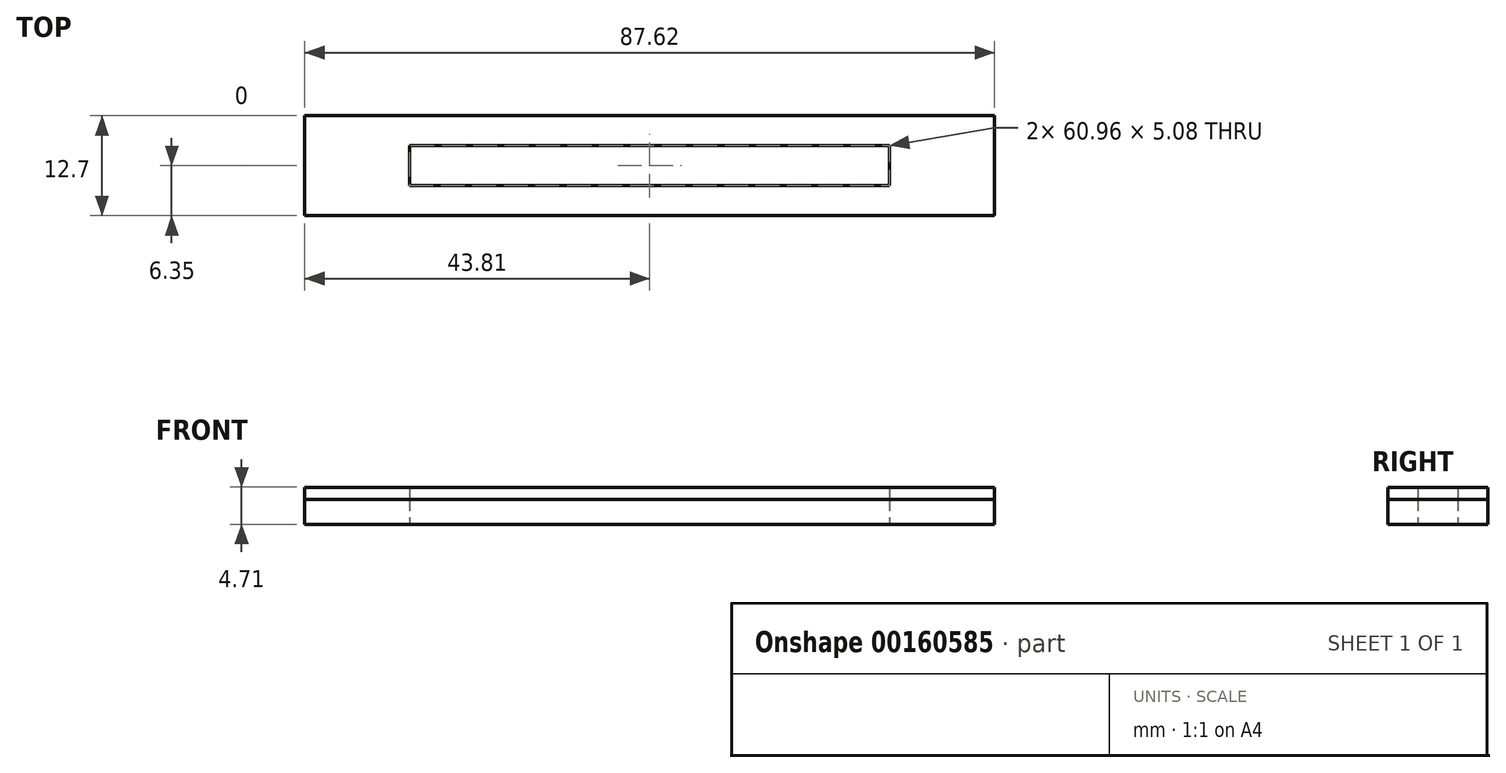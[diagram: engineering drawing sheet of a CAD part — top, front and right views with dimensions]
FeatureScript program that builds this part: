
annotation { "Feature Type Name" : "Feature", "Feature Type Description" : "" }
export const myFeature = defineFeature(function(context is Context, id is Id, definition is map)
    precondition{}
    {
        {
            var Q0;
            Q0=qCreatedBy(makeId("Top.planeOp"),FACE);
            var sketch = newSketch(context, id + "F0", { "sketchPlane" : qUnion([Q0])});
            skLineSegment(sketch, "E0.bottom", {"start": v(66.04, 6.35) * mm, "end": v(-66.04, 6.35) * mm});
            skLineSegment(sketch, "E0.top", {"start": v(66.04, -6.35) * mm, "end": v(-66.04, -6.35) * mm});
            skLineSegment(sketch, "E0.left", {"start": v(66.04, 6.35) * mm, "end": v(66.04, -6.35) * mm});
            skLineSegment(sketch, "E0.right", {"start": v(-66.04, 6.35) * mm, "end": v(-66.04, -6.35) * mm});
            skPoint(sketch, "E0.middle", {"position": v(0, 0) * mm});
            skSolve(sketch);
        }
        {
            var Q0;
            Q0 = qSketchRegion(id + "F0", true);
            extrude(context, id + "F1", {"entities" : qUnion([Q0]), "oppositeDirection" : true, "depth" : 3.17 * mm});
        }
        {
            var Q0;
            Q0=makeQuery(id+"F1.opExtrude","CAP_FACE",FACE,{"disambiguationData":[OSD([sQuery(id+"F0.wireOp",EDGE,"E0.bottom"),sQuery(id+"F0.wireOp",EDGE,"E0.top"),sQuery(id+"F0.wireOp",EDGE,"E0.left"),sQuery(id+"F0.wireOp",EDGE,"E0.right")])],"isStart":true});
            extrude(context, id + "F2", {"entities" : qUnion([Q0]), "depth" : (1.4 + (1 / 8)) * mm});
        }
        {
            var Q0;
            Q0=makeQuery(id+"F2.opExtrude","CAP_FACE",FACE,{"disambiguationData":[OSD([sQuery(id+"F0.wireOp",EDGE,"E0.bottom"),sQuery(id+"F0.wireOp",EDGE,"E0.top"),sQuery(id+"F0.wireOp",EDGE,"E0.left"),sQuery(id+"F0.wireOp",EDGE,"E0.right")])],"isStart":false});
            var sketch = newSketch(context, id + "F3", { "sketchPlane" : qUnion([Q0])});
            skLineSegment(sketch, "E1.bottom", {"start": v(43.82, 6.35) * mm, "end": v(-43.81, 6.35) * mm});
            skLineSegment(sketch, "E1.top", {"start": v(43.82, -6.35) * mm, "end": v(-43.81, -6.35) * mm});
            skLineSegment(sketch, "E1.left", {"start": v(43.82, 6.35) * mm, "end": v(43.82, -6.35) * mm});
            skLineSegment(sketch, "E1.right", {"start": v(-43.81, 6.35) * mm, "end": v(-43.81, -6.35) * mm});
            skSolve(sketch);
        }
        {
            var Q0;
            {var subQ0=sQuery(id+"F3.wireOp",EDGE,"E1.right");Q0=makeQuery(id+"F3.imprint","IMPRINT",FACE,{"disambiguationData":[TD([[makeQuery(id+"F3.imprint","IMPRINT",EDGE,{"derivedFrom":subQ0}),-1.0]])]});}
            var Q1;
            {var subQ0=sQuery(id+"F3.wireOp",EDGE,"E1.left");Q1=makeQuery(id+"F3.imprint","IMPRINT",FACE,{"disambiguationData":[TD([[makeQuery(id+"F3.imprint","IMPRINT",EDGE,{"derivedFrom":subQ0}),1.0]])]});}
            extrude(context, id + "F4", {"entities" : qUnion([Q0, Q1]), "operationType" : NewBodyOperationType.REMOVE, "oppositeDirection" : true, "depth" : 35.56 * mm});
        }
        {
            var Q0;
            Q0=makeQuery(id+"F2.opExtrude","SWEPT_FACE",FACE,{"disambiguationData":[OSD([sQuery(id+"F0.wireOp",EDGE,"E0.top")])]});
            var sketch = newSketch(context, id + "F5", { "sketchPlane" : qUnion([Q0])});
            skLineSegment(sketch, "E2.bottom", {"start": v(40.64, 35.56) * mm, "end": v(-40.64, 35.56) * mm});
            skLineSegment(sketch, "E2.top", {"start": v(40.64, 0) * mm, "end": v(-40.64, 0) * mm});
            skLineSegment(sketch, "E2.left", {"start": v(40.64, 35.56) * mm, "end": v(40.64, 0) * mm});
            skLineSegment(sketch, "E2.right", {"start": v(-40.64, 35.56) * mm, "end": v(-40.64, 0) * mm});
            skSolve(sketch);
        }
        {
            var Q0;
            Q0=makeQuery(id+"F5.imprint","IMPRINT",FACE,{"disambiguationData":[TD([[makeQuery(id+"F5.imprint","IMPRINT",EDGE,{"derivedFrom":sQuery(id+"F5.wireOp",EDGE,"E2.bottom")}),1.0]])]});
            extrude(context, id + "F6", {"entities" : qUnion([Q0]), "operationType" : NewBodyOperationType.REMOVE, "endBound" : BoundingType.THROUGH_ALL, "oppositeDirection" : true, "depth" : 25.4 * mm});
        }
        {
            var Q0;
            Q0=qCreatedBy(makeId("Top.planeOp"),FACE);
            var sketch = newSketch(context, id + "F7", { "sketchPlane" : qUnion([Q0])});
            skLineSegment(sketch, "E3.bottom", {"start": v(30.48, 2.54) * mm, "end": v(-30.48, 2.54) * mm});
            skLineSegment(sketch, "E3.top", {"start": v(30.48, -2.54) * mm, "end": v(-30.48, -2.54) * mm});
            skLineSegment(sketch, "E3.left", {"start": v(30.48, 2.54) * mm, "end": v(30.48, -2.54) * mm});
            skLineSegment(sketch, "E3.right", {"start": v(-30.48, 2.54) * mm, "end": v(-30.48, -2.54) * mm});
            skPoint(sketch, "E3.middle", {"position": v(0, 0) * mm});
            skCircle(sketch, "E4", {"center": v(55.88, 0) * mm, "radius": 3.18 * mm});
            skCircle(sketch, "E5", {"center": v(-55.88, 0) * mm, "radius": 3.18 * mm});
            skSolve(sketch);
        }
        {
            var Q0;
            Q0=makeQuery(id+"F7.imprint","IMPRINT",FACE,{"disambiguationData":[TD([[makeQuery(id+"F7.imprint","IMPRINT",EDGE,{"derivedFrom":sQuery(id+"F7.wireOp",EDGE,"E5")}),1.0]])]});
            var Q1;
            Q1=makeQuery(id+"F7.imprint","IMPRINT",FACE,{"disambiguationData":[TD([[makeQuery(id+"F7.imprint","IMPRINT",EDGE,{"derivedFrom":sQuery(id+"F7.wireOp",EDGE,"E3.bottom")}),1.0]])]});
            var Q2;
            Q2=makeQuery(id+"F7.imprint","IMPRINT",FACE,{"disambiguationData":[TD([[makeQuery(id+"F7.imprint","IMPRINT",EDGE,{"derivedFrom":sQuery(id+"F7.wireOp",EDGE,"E4")}),1.0]])]});
            extrude(context, id + "F8", {"entities" : qUnion([Q0, Q1, Q2]), "operationType" : NewBodyOperationType.REMOVE, "endBound" : BoundingType.THROUGH_ALL, "depth" : 25.4 * mm, "hasSecondDirection" : true, "secondDirectionBound" : SecondDirectionBoundingType.THROUGH_ALL, "secondDirectionOppositeDirection" : true, "secondDirectionDepth" : 25.4 * mm});
        }
        {
            var Q0;
            Q0=makeQuery(id+"F4.boolean.opBoolean","COPY",FACE,{"derivedFrom":makeQuery(id+"F4.opExtrude","SWEPT_FACE",FACE,{"disambiguationData":[OSD([sQuery(id+"F3.wireOp",EDGE,"E1.right")])]})});
            var sketch = newSketch(context, id + "F9", { "sketchPlane" : qUnion([Q0])});
            skLineSegment(sketch, "E6.bottom", {"start": v(2.54, 28.57) * mm, "end": v(-2.54, 28.57) * mm});
            skLineSegment(sketch, "E6.top", {"start": v(2.54, 13.33) * mm, "end": v(-2.54, 13.33) * mm});
            skLineSegment(sketch, "E6.left", {"start": v(2.54, 28.57) * mm, "end": v(2.54, 13.33) * mm});
            skLineSegment(sketch, "E6.right", {"start": v(-2.54, 28.57) * mm, "end": v(-2.54, 13.33) * mm});
            skPoint(sketch, "E6.middle", {"position": v(0, 20.95) * mm});
            skSolve(sketch);
        }
        {
            var Q0;
            Q0 = qSketchRegion(id + "F9", true);
            extrude(context, id + "F10", {"entities" : qUnion([Q0]), "operationType" : NewBodyOperationType.REMOVE, "endBound" : BoundingType.THROUGH_ALL, "oppositeDirection" : true, "depth" : 25.4 * mm});
        }
    });
